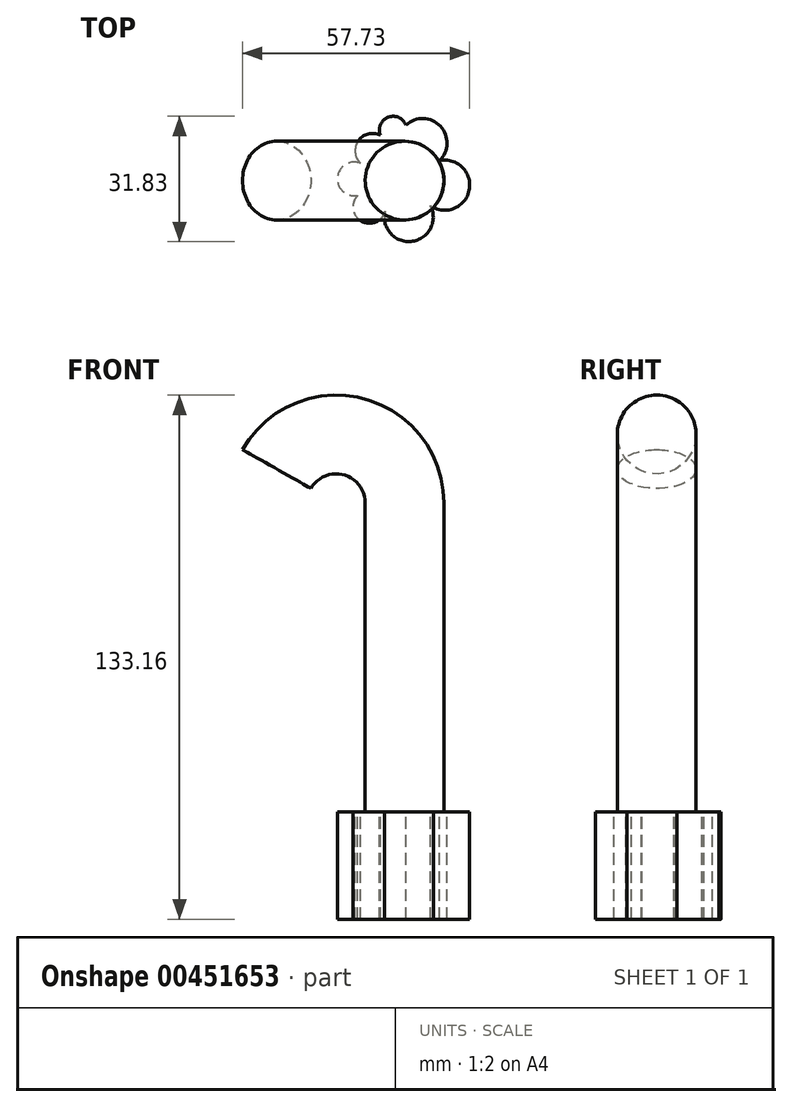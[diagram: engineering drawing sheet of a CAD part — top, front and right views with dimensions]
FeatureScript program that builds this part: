
annotation { "Feature Type Name" : "Feature", "Feature Type Description" : "" }
export const myFeature = defineFeature(function(context is Context, id is Id, definition is map)
    precondition{}
    {
        {
            var Q0;
            Q0=qCreatedBy(makeId("Top.planeOp"),FACE);
            var sketch = newSketch(context, id + "F0", { "sketchPlane" : qUnion([Q0])});
            skCircle(sketch, "E0", {"center": v(0, 0) * mm, "radius": 10 * mm});
            skSolve(sketch);
        }
        {
            var Q0;
            Q0=qCreatedBy(makeId("Front.planeOp"),FACE);
            var sketch = newSketch(context, id + "F1", { "sketchPlane" : qUnion([Q0])});
            skLineSegment(sketch, "E1", {"start": v(0, 0) * mm, "end": v(0, 78.59) * mm});
            skArc(sketch, "E2", {"start": v(0, 78.59) * mm, "mid": v(-12.93, 95.38) * mm, "end": v(-32.48, 87.17) * mm});
            skSolve(sketch);
        }
        {
            var Q0;
            Q0=makeQuery(id+"F0.imprint","IMPRINT",FACE,{"disambiguationData":[TD([[makeQuery(id+"F0.imprint","IMPRINT",EDGE,{"derivedFrom":sQuery(id+"F0.wireOp",EDGE,"d4263764-7886-4802-9c4c-ae2b7f0093ff.0")}),-1.0]])]});
            var Q1;
            Q1=makeQuery(id+"F0.imprint","IMPRINT",FACE,{"disambiguationData":[TD([[makeQuery(id+"F0.imprint","IMPRINT",EDGE,{"derivedFrom":sQuery(id+"F0.wireOp",EDGE,"E0")}),1.0]])]});
            var Q2;
            Q2=sQuery(id+"F1.wireOp",EDGE,"E1");
            var Q3;
            Q3=sQuery(id+"F1.wireOp",EDGE,"E2");
            sweep(context, id + "F2", {"profiles" : qUnion([Q0, Q1]), "path" : qUnion([Q2, Q3])});
        }
        {
            var Q0;
            Q0=qCreatedBy(makeId("Top.planeOp"),FACE);
            var sketch = newSketch(context, id + "F3", { "sketchPlane" : qUnion([Q0])});
            skCircle(sketch, "E3", {"center": v(0, 0) * mm, "radius": 5.94 * mm});
            skSolve(sketch);
        }
        {
            var Q0;
            Q0=makeQuery(id+"F3.imprint","IMPRINT",FACE,{"disambiguationData":[TD([[makeQuery(id+"F3.imprint","IMPRINT",EDGE,{"derivedFrom":sQuery(id+"F3.wireOp",EDGE,"E3")}),1.0]])]});
            var sketch = newSketch(context, id + "F4", { "sketchPlane" : qUnion([Q0])});
            skArc(sketch, "E4", {"start": v(5.53, 3.45) * mm, "mid": v(6.63, 15.42) * mm, "end": v(0, 5.39) * mm});
            skArc(sketch, "E5", {"start": v(4.58, -4.18) * mm, "mid": v(16.55, -1.16) * mm, "end": v(4.58, 1.86) * mm});
            skArc(sketch, "E6", {"start": v(-2.4, -4.18) * mm, "mid": v(1.09, -15.5) * mm, "end": v(4.58, -4.18) * mm});
            skArc(sketch, "E7", {"start": v(-9.74, -2.59) * mm, "mid": v(-12, -9.5) * mm, "end": v(-4.93, -7.79) * mm});
            skArc(sketch, "E8", {"start": v(-9.74, 3.45) * mm, "mid": v(-17.07, 0.43) * mm, "end": v(-9.74, -2.59) * mm});
            skArc(sketch, "E9", {"start": v(-4.19, 9.57) * mm, "mid": v(-11.41, 10.54) * mm, "end": v(-9.74, 3.45) * mm});
            skArc(sketch, "E10", {"start": v(-1.62, 9.57) * mm, "mid": v(-2.9, 16.33) * mm, "end": v(-4.19, 9.57) * mm});
            skSolve(sketch);
        }
        {
            var Q0;
            Q0 = qSketchRegion(id + "F4", true);
            extrude(context, id + "F5", {"entities" : qUnion([Q0]), "operationType" : NewBodyOperationType.ADD, "oppositeDirection" : true, "depth" : 27.2 * mm, "offsetDistance" : 25 * mm});
        }
    });
